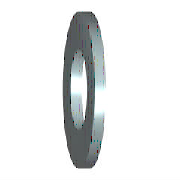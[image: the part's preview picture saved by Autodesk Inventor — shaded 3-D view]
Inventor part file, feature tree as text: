
AUTODESK INVENTOR PART (.ipt)
format: ipt  version: 2023.4 (Build 274418000, 418)  size: 108,544 bytes
history: native  units: mm (DEFAULTED — no unit token found)
features: other x1, plane x1
ambient origin geometry x7: Origin, YZ Plane, XY Plane, X Axis, Y Axis, Z Axis, Center Point
bodies: Solid1 (feature_tree), Body (feature_tree)
feature tree (2):
  other  "Work Axis1"
  plane  "Work Plane1"
